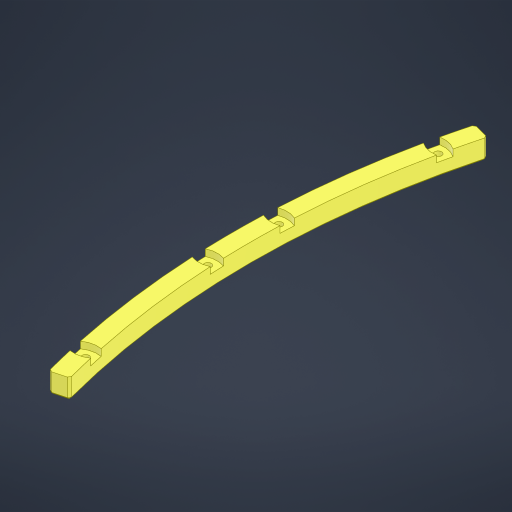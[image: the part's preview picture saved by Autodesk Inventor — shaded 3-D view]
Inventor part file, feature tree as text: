
AUTODESK INVENTOR PART (.ipt)
format: ipt  version: 2023.2 (Build 272271030, 271C)  size: 241,664 bytes
history: native  units: mm
features: extrude x2, sketch x1, chamfer x1
ambient origin geometry x8: Origin, YZ Plane, XZ Plane, XY Plane, X Axis, Y Axis, Z Axis, Center Point
bodies: Volumenkörper1 (feature_tree)
feature tree (4):
  sketch  "Skizze1"  dims[d1=7.8mm d2=30.0deg d4=1.745329mm d5=0.872665mm d6=1.745329mm d7=3.2mm d8=6.0mm d9=6.0mm d10=0.0mm d11=3.0mm d12=0.0mm d13=1.0mm d14=2.0mm d15=45.0deg d17=10.0mm d18=366.0mm d19=10.0mm]
  extrude  "Extrusion1"  TaperAngle=30.0deg  [1 undecoded]
  extrude  "Extrusion2"  Depth=10.0mm
  chamfer  "Fase1"  Distance=0.872665mm
note: 1 required parameter value undecoded (feature->parameter linkage not recoverable at this tier; creation-order binding heuristic only, values carry confidence <= 0.55)
